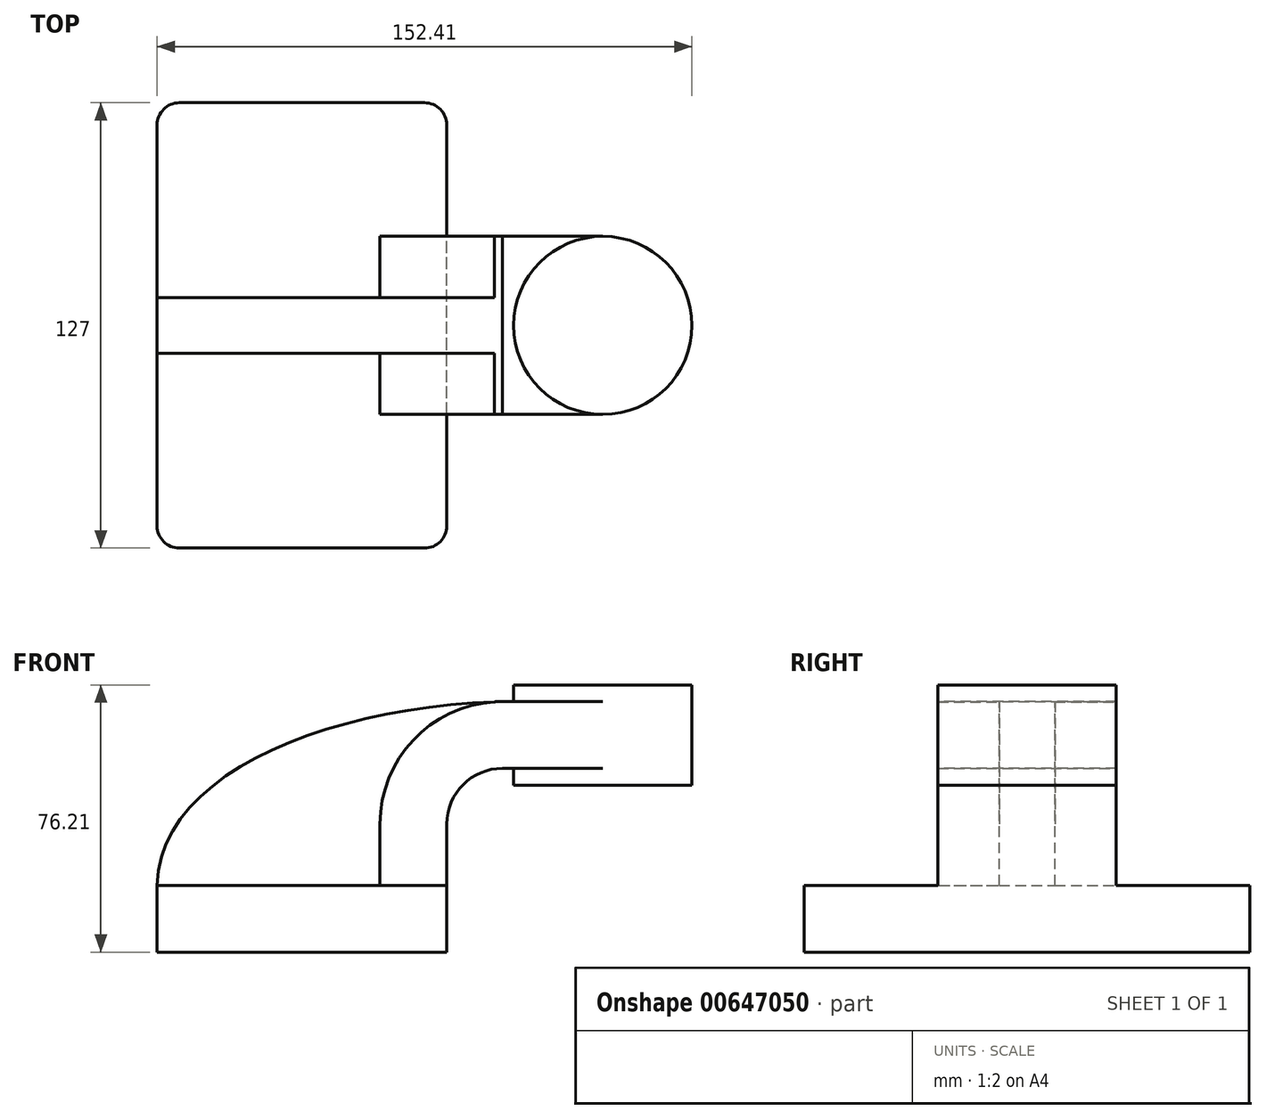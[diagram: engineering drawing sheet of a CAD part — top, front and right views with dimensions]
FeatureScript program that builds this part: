
annotation { "Feature Type Name" : "Feature", "Feature Type Description" : "" }
export const myFeature = defineFeature(function(context is Context, id is Id, definition is map)
    precondition{}
    {
        {
            var Q0;
            Q0=qCreatedBy(makeId("Front.planeOp"),FACE);
            var sketch = newSketch(context, id + "F0", { "sketchPlane" : qUnion([Q0])});
            skLineSegment(sketch, "E0.bottom", {"start": v(-41.28, 9.52) * mm, "end": v(41.27, 9.53) * mm});
            skLineSegment(sketch, "E0.top", {"start": v(-41.28, -9.52) * mm, "end": v(41.28, -9.52) * mm});
            skLineSegment(sketch, "E0.left", {"start": v(-41.28, 9.52) * mm, "end": v(-41.28, -9.53) * mm});
            skLineSegment(sketch, "E0.right", {"start": v(41.27, 9.53) * mm, "end": v(41.28, -9.52) * mm});
            skPoint(sketch, "E0.middle", {"position": v(0, 0) * mm});
            skLineSegment(sketch, "E1.bottom", {"start": v(111.12, 38.1) * mm, "end": v(60.32, 38.1) * mm});
            skLineSegment(sketch, "E1.top", {"start": v(111.12, 66.68) * mm, "end": v(60.32, 66.68) * mm});
            skLineSegment(sketch, "E1.left", {"start": v(111.12, 38.1) * mm, "end": v(111.12, 66.68) * mm});
            skLineSegment(sketch, "E1.right", {"start": v(60.32, 38.1) * mm, "end": v(60.32, 66.67) * mm});
            skPoint(sketch, "E1.middle", {"position": v(85.72, 52.39) * mm});
            skLineSegment(sketch, "E2", {"start": v(41.27, 9.53) * mm, "end": v(41.27, 27) * mm});
            skArc(sketch, "E3", {"start": v(41.27, 27) * mm, "mid": v(45.92, 38.23) * mm, "end": v(57.15, 42.88) * mm});
            skLineSegment(sketch, "E4", {"start": v(57.15, 42.88) * mm, "end": v(85.72, 42.88) * mm});
            skLineSegment(sketch, "E5.0", {"start": v(57.15, 61.93) * mm, "end": v(85.72, 61.93) * mm});
            skArc(sketch, "E5.1", {"start": v(22.22, 27) * mm, "mid": v(32.45, 51.7) * mm, "end": v(57.15, 61.93) * mm});
            skLineSegment(sketch, "E5.2", {"start": v(22.22, 9.53) * mm, "end": v(22.22, 27) * mm});
            skPoint(sketch, "E6", {"position": v(85.72, 66.68) * mm});
            skLineSegment(sketch, "E7", {"start": v(85.73, 66.68) * mm, "end": v(85.72, 38.1) * mm});
            skFitSpline(sketch, "E8", {"points": [v(-41.28, 9.52) * mm, v(57.15, 61.93) * mm], "startDerivative": vector(2.14, 97.3) * mm, "endDerivative": vector(145.8, 3.95) * mm});
            skSolve(sketch);
        }
        {
            var Q0;
            Q0=makeQuery(id+"F0.imprint","IMPRINT",FACE,{"disambiguationData":[TD([[makeQuery(id+"F0.imprint","IMPRINT",EDGE,{"derivedFrom":sQuery(id+"F0.wireOp",EDGE,"E0.top")}),1.0]])]});
            extrude(context, id + "F1", {"entities" : qUnion([Q0]), "endBound" : BoundingType.SYMMETRIC, "depth" : 127 * mm, "offsetDistance" : 25.4 * mm});
        }
        {
            var Q0;
            {var subQ1=sQuery(id+"F0.wireOp",EDGE,"E2");Q0=makeQuery(id+"F0.imprint","IMPRINT",FACE,{"disambiguationData":[TD([[makeQuery(id+"F0.imprint","IMPRINT",EDGE,{"derivedFrom":subQ1}),1.0]])]});}
            var Q1;
            {var subQ0=sQuery(id+"F0.wireOp",EDGE,"E4");var subQ1=sQuery(id+"F0.wireOp",EDGE,"E1.right");var subQ2=makeQuery(id+"F0.imprint","INTERSECT",VERTEX,{"derivedFrom":[subQ1,subQ0]});Q1=makeQuery(id+"F0.imprint","IMPRINT",FACE,{"disambiguationData":[TD([[makeQuery(id+"F0.imprint","IMPRINT",EDGE,{"disambiguationData":[TD([[subQ2,-1.0]])],"derivedFrom":subQ1}),-1.0]])]});}
            extrude(context, id + "F2", {"entities" : qUnion([Q0, Q1]), "operationType" : NewBodyOperationType.ADD, "endBound" : BoundingType.SYMMETRIC, "depth" : 50.8 * mm, "offsetDistance" : 25.4 * mm});
        }
        {
            var Q0;
            {var subQ3=sQuery(id+"F0.wireOp",EDGE,"E5.2");Q0=makeQuery(id+"F0.imprint","IMPRINT",FACE,{"disambiguationData":[TD([[makeQuery(id+"F0.imprint","IMPRINT",EDGE,{"derivedFrom":subQ3}),1.0]])]});}
            extrude(context, id + "F3", {"entities" : qUnion([Q0]), "operationType" : NewBodyOperationType.ADD, "endBound" : BoundingType.SYMMETRIC, "depth" : 15.88 * mm, "offsetDistance" : 25.4 * mm});
        }
        {
            var Q0;
            {var subQ0=sQuery(id+"F0.wireOp",EDGE,"E1.left");Q0=makeQuery(id+"F0.imprint","IMPRINT",FACE,{"disambiguationData":[TD([[makeQuery(id+"F0.imprint","IMPRINT",EDGE,{"derivedFrom":subQ0}),1.0]])]});}
            var Q1;
            Q1=sQuery(id+"F0.wireOp",EDGE,"E7");
            revolve(context, id + "F4", {"operationType" : NewBodyOperationType.ADD, "entities" : qUnion([Q0]), "axis" : qUnion([Q1]), "revolveType" : RevolveType.FULL});
        }
        {
            var Q0;
            Q0=makeQuery(id+"F1.opExtrude","CAP_EDGE",EDGE,{"disambiguationData":[OSD([sQuery(id+"F0.wireOp",EDGE,"E0.right")])],"isStart":false});
            var Q1;
            Q1=makeQuery(id+"F1.opExtrude","CAP_EDGE",EDGE,{"disambiguationData":[OSD([sQuery(id+"F0.wireOp",EDGE,"E0.left")])],"isStart":false});
            var Q2;
            Q2=makeQuery(id+"F1.opExtrude","CAP_EDGE",EDGE,{"disambiguationData":[OSD([sQuery(id+"F0.wireOp",EDGE,"E0.right")])],"isStart":true});
            var Q3;
            Q3=makeQuery(id+"F1.opExtrude","CAP_EDGE",EDGE,{"disambiguationData":[OSD([sQuery(id+"F0.wireOp",EDGE,"E0.left")])],"isStart":true});
            fillet(context, id + "F5", {"entities" : qUnion([Q0, Q1, Q2, Q3]), "radius" : 6.35 * mm, "tangentPropagation" : true, "allowEdgeOverflow" : false});
        }
    });
